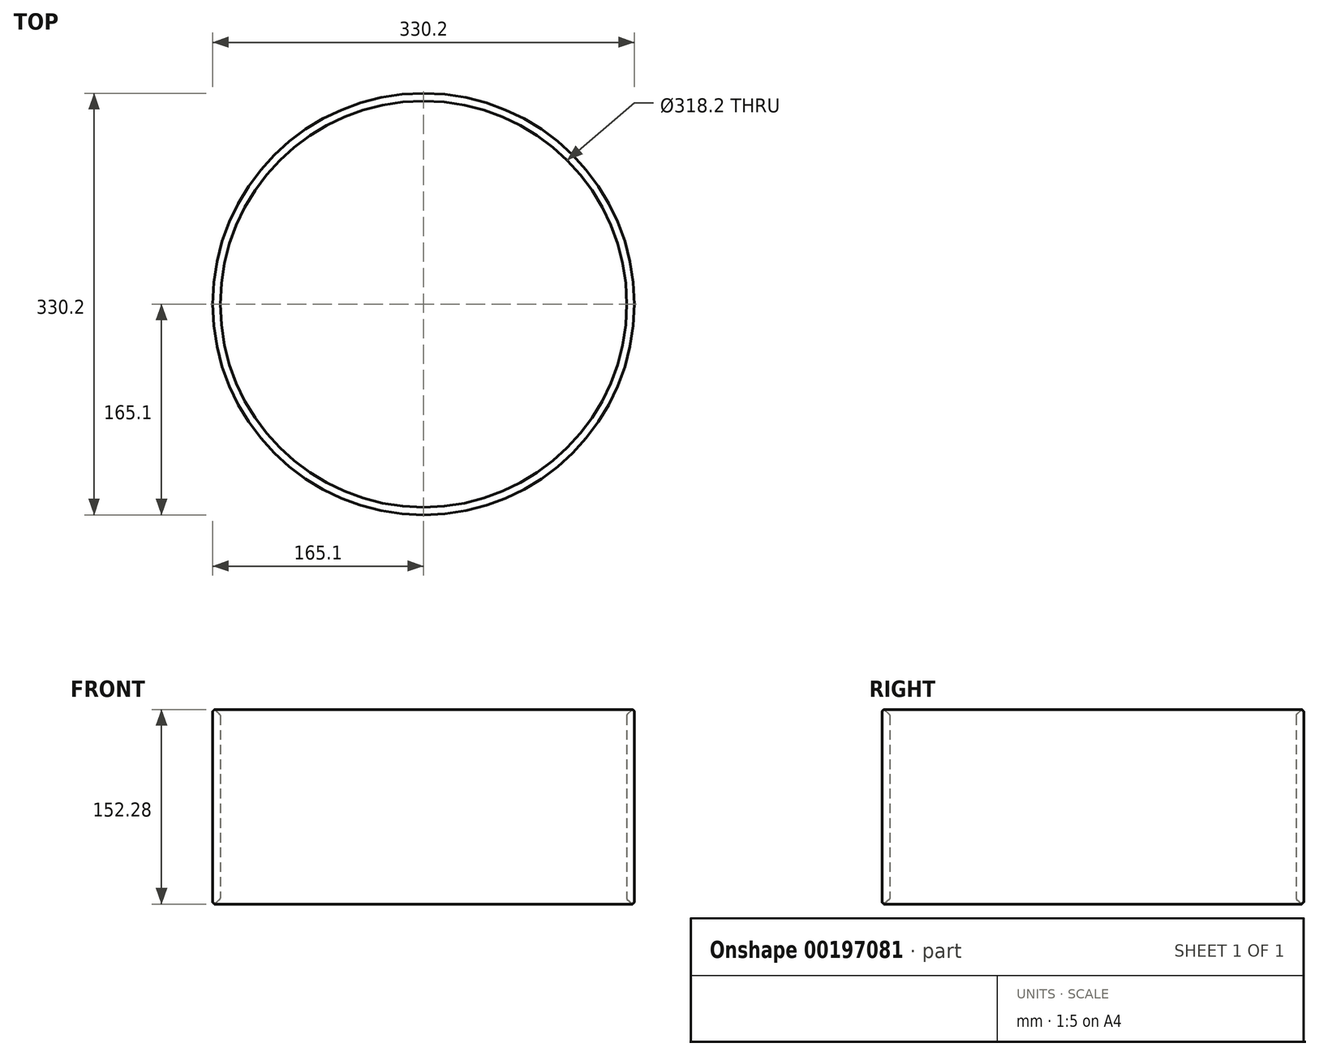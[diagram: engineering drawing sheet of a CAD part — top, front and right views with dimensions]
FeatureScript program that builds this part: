
annotation { "Feature Type Name" : "Feature", "Feature Type Description" : "" }
export const myFeature = defineFeature(function(context is Context, id is Id, definition is map)
    precondition{}
    {
        {
            var Q0;
            Q0=qCreatedBy(makeId("Top.planeOp"),FACE);
            var sketch = newSketch(context, id + "F0", { "sketchPlane" : qUnion([Q0])});
            skCircle(sketch, "E0", {"center": v(0, 0) * mm, "radius": 165.1 * mm});
            skCircle(sketch, "E1.0", {"center": v(0, 0) * mm, "radius": 159.1 * mm});
            skSolve(sketch);
        }
        {
            var Q0;
            Q0=makeQuery(id+"F0.imprint","IMPRINT",FACE,{"disambiguationData":[TD([[makeQuery(id+"F0.imprint","IMPRINT",EDGE,{"derivedFrom":sQuery(id+"F0.wireOp",EDGE,"E0")}),1.0]])]});
            extrude(context, id + "F1", {"entities" : qUnion([Q0]), "endBound" : BoundingType.SYMMETRIC, "depth" : 152.4 * mm});
        }
        {
            var Q0;
            Q0=qCreatedBy(makeId("Front.planeOp"),FACE);
            var sketch = newSketch(context, id + "F2", { "sketchPlane" : qUnion([Q0])});
            skLineSegment(sketch, "E2", {"start": v(-165.1, -76.2) * mm, "end": v(-165.1, 76.2) * mm});
            skLineSegment(sketch, "E3", {"start": v(-165.1, -76.2) * mm, "end": v(-165.1, 74.58) * mm});
            skLineSegment(sketch, "E4", {"start": v(-165.1, 68.34) * mm, "end": v(-165.1, 76.2) * mm});
            skLineSegment(sketch, "E5", {"start": v(-159.1, 71.58) * mm, "end": v(-159.1, 70.61) * mm});
            skLineSegment(sketch, "E6", {"start": v(-165.01, 74.79) * mm, "end": v(-163.7, 76.1) * mm});
            skLineSegment(sketch, "E7", {"start": v(-163.5, 76.1) * mm, "end": v(-159.42, 72.3) * mm});
            skPoint(sketch, "E8.newPointA", {"position": v(-165.1, 74.7) * mm});
            skPoint(sketch, "E8.newPointB", {"position": v(-165.1, 76.2) * mm});
            skArc(sketch, "E8.filletArc", {"start": v(-165.01, 74.79) * mm, "mid": v(-165.08, 74.7) * mm, "end": v(-165.1, 74.58) * mm});
            skPoint(sketch, "E9.visualSharp", {"position": v(-163.6, 76.2) * mm});
            skArc(sketch, "E9.filletArc", {"start": v(-163.5, 76.1) * mm, "mid": v(-163.6, 76.14) * mm, "end": v(-163.7, 76.1) * mm});
            skPoint(sketch, "E10.newPointA", {"position": v(-158.77, 71.7) * mm});
            skPoint(sketch, "E10.newPointB", {"position": v(-159.1, 76.2) * mm});
            skArc(sketch, "E10.filletArc", {"start": v(-159.1, 71.58) * mm, "mid": v(-159.18, 71.97) * mm, "end": v(-159.42, 72.3) * mm});
            skLineSegment(sketch, "E11", {"start": v(-165.1, 76.2) * mm, "end": v(-159.1, 76.2) * mm});
            skLineSegment(sketch, "E12", {"start": v(-159.1, 71.58) * mm, "end": v(-159.1, 76.2) * mm});
            skLineSegment(sketch, "E13", {"start": v(0, 76.88) * mm, "end": v(0, -76.29) * mm, "construction": true});
            skArc(sketch, "E14.MirrorCS", {"start": v(-163.5, -76.1) * mm, "mid": v(-163.6, -76.14) * mm, "end": v(-163.7, -76.1) * mm});
            skLineSegment(sketch, "E15.MirrorCS", {"start": v(-165.01, -74.79) * mm, "end": v(-163.7, -76.1) * mm});
            skArc(sketch, "E16.MirrorCS", {"start": v(-165.01, -74.79) * mm, "mid": v(-165.08, -74.7) * mm, "end": v(-165.1, -74.58) * mm});
            skArc(sketch, "E17.MirrorCS", {"start": v(-159.1, -71.58) * mm, "mid": v(-159.18, -71.97) * mm, "end": v(-159.42, -72.3) * mm});
            skLineSegment(sketch, "E18.MirrorCS", {"start": v(-159.1, -71.58) * mm, "end": v(-159.1, -70.61) * mm});
            skLineSegment(sketch, "E19.MirrorCS", {"start": v(-165.1, -76.2) * mm, "end": v(-159.1, -76.2) * mm});
            skLineSegment(sketch, "E20.MirrorCS", {"start": v(-159.1, -71.58) * mm, "end": v(-159.1, -76.2) * mm});
            skLineSegment(sketch, "E21.MirrorCS", {"start": v(-165.1, -68.34) * mm, "end": v(-165.1, -76.2) * mm});
            skLineSegment(sketch, "E22.MirrorCS", {"start": v(-163.5, -76.1) * mm, "end": v(-159.42, -72.3) * mm});
            skPoint(sketch, "E23.MirrorP", {"position": v(-163.6, -76.2) * mm});
            skPoint(sketch, "E24.MirrorP", {"position": v(-165.1, -76.2) * mm});
            skPoint(sketch, "E25.MirrorP", {"position": v(-165.1, -74.7) * mm});
            skPoint(sketch, "E26.MirrorP", {"position": v(-159.1, -76.2) * mm});
            skPoint(sketch, "E27.MirrorP", {"position": v(-158.77, -71.7) * mm});
            skSolve(sketch);
        }
        {
            var Q0;
            Q0 = qSketchRegion(id + "F2", true);
            var Q1;
            Q1=sQuery(id+"F2.wireOp",EDGE,"E13");
            revolve(context, id + "F3", {"operationType" : NewBodyOperationType.REMOVE, "entities" : qUnion([Q0]), "axis" : qUnion([Q1]), "revolveType" : RevolveType.FULL, "oppositeDirection" : true});
        }
    });
